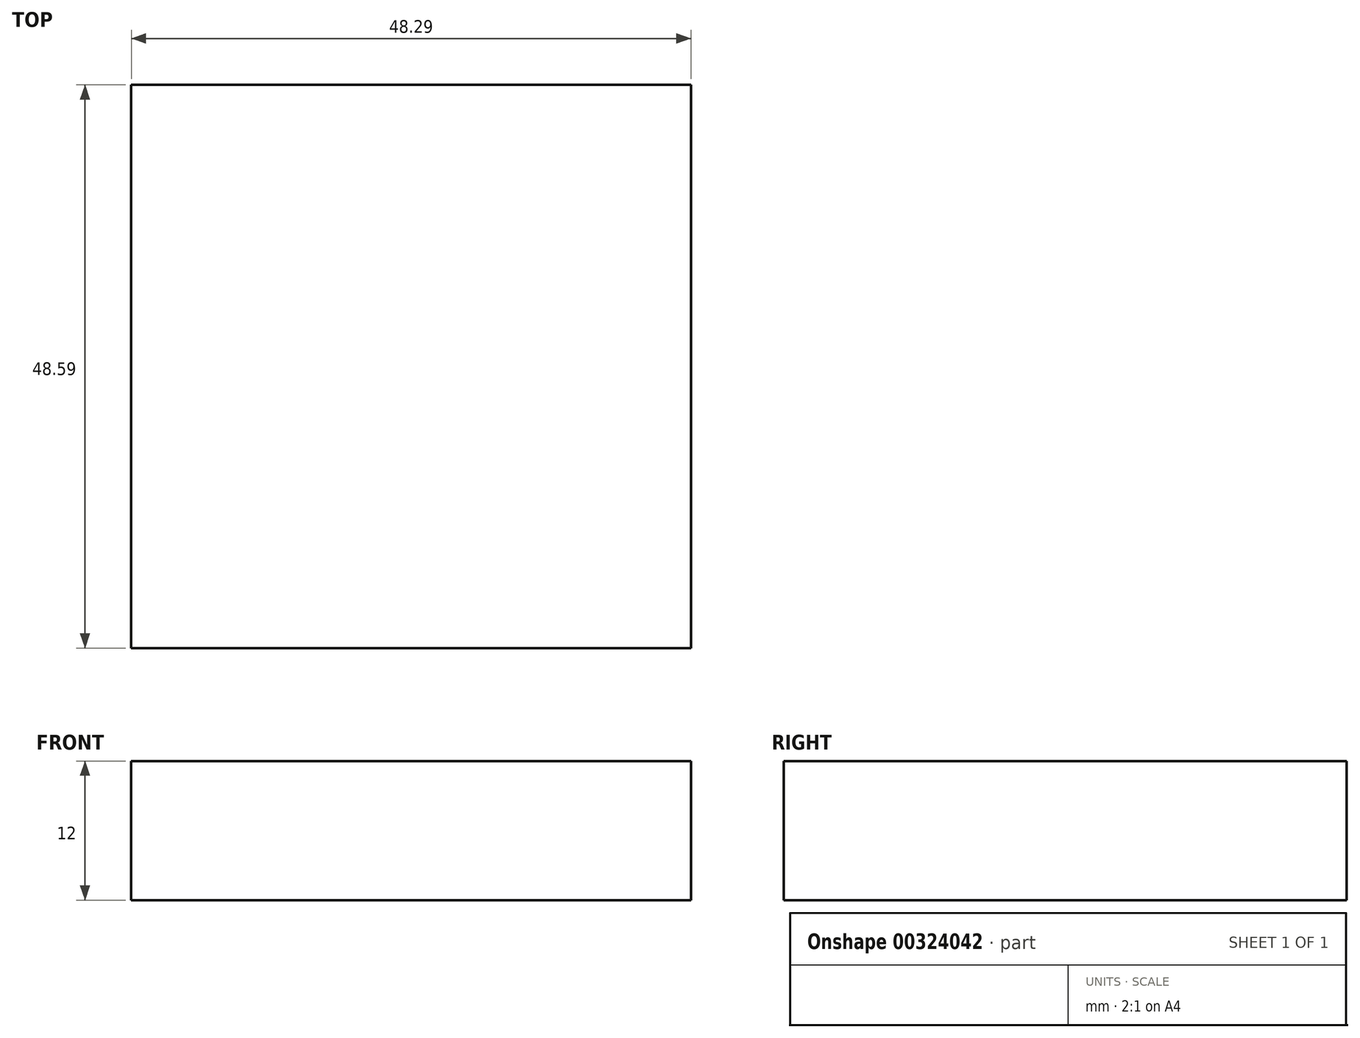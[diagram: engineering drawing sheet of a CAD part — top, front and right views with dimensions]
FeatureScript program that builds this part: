
annotation { "Feature Type Name" : "Feature", "Feature Type Description" : "" }
export const myFeature = defineFeature(function(context is Context, id is Id, definition is map)
    precondition{}
    {
        {
            var Q0;
            Q0=qCreatedBy(makeId("Top.planeOp"),FACE);
            var sketch = newSketch(context, id + "F0", { "sketchPlane" : qUnion([Q0])});
            skLineSegment(sketch, "E0", {"start": v(-55.51, -67.48) * mm, "end": v(5.08, 0) * mm});
            skLineSegment(sketch, "E1", {"start": v(5.08, 0) * mm, "end": v(50.72, -78.12) * mm});
            skLineSegment(sketch, "E2", {"start": v(50.72, -78.12) * mm, "end": v(-55.51, -67.48) * mm});
            skCircle(sketch, "E3", {"center": v(-17.58, 42.14) * mm, "radius": 39.65 * mm});
            skLineSegment(sketch, "E4.bottom", {"start": v(-63.64, -33.93) * mm, "end": v(-111.93, -33.93) * mm});
            skLineSegment(sketch, "E4.top", {"start": v(-63.64, 14.66) * mm, "end": v(-111.93, 14.66) * mm});
            skLineSegment(sketch, "E4.left", {"start": v(-63.64, -33.93) * mm, "end": v(-63.64, 14.66) * mm});
            skLineSegment(sketch, "E4.right", {"start": v(-111.93, -33.93) * mm, "end": v(-111.93, 14.66) * mm});
            skPoint(sketch, "E4.middle", {"position": v(-87.78, -9.63) * mm});
            skSolve(sketch);
        }
        {
            var Q0;
            Q0=makeQuery(id+"F0.imprint","IMPRINT",FACE,{"disambiguationData":[TD([[makeQuery(id+"F0.imprint","IMPRINT",EDGE,{"derivedFrom":sQuery(id+"F0.wireOp",EDGE,"E4.bottom")}),-1.0]])]});
            extrude(context, id + "F1", {"entities" : qUnion([Q0]), "depth" : 12 * mm});
        }
    });
